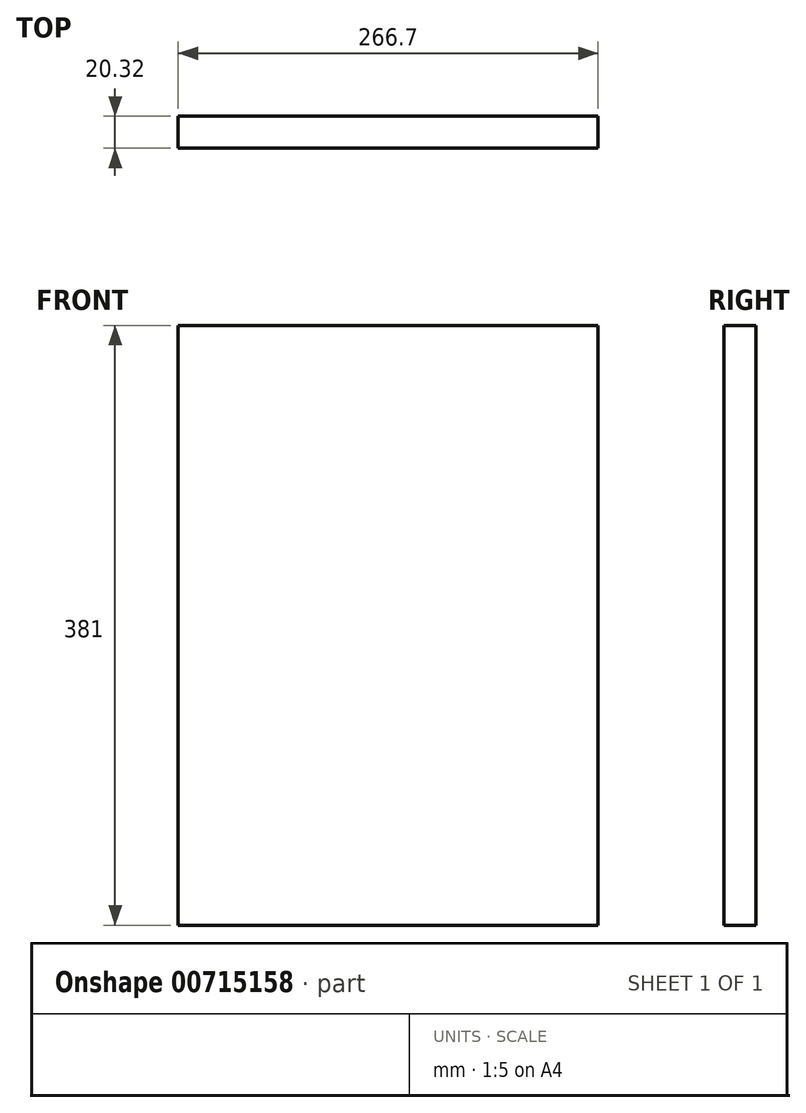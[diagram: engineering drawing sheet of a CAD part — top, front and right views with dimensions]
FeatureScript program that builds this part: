
annotation { "Feature Type Name" : "Feature", "Feature Type Description" : "" }
export const myFeature = defineFeature(function(context is Context, id is Id, definition is map)
    precondition{}
    {
        {
            var Q0;
            Q0=qCreatedBy(makeId("Front.planeOp"),FACE);
            var sketch = newSketch(context, id + "F0", { "sketchPlane" : qUnion([Q0])});
            skLineSegment(sketch, "E0.bottom", {"start": v(-142.27, 239.95) * mm, "end": v(124.43, 239.95) * mm});
            skLineSegment(sketch, "E0.top", {"start": v(-142.27, -141.05) * mm, "end": v(124.43, -141.05) * mm});
            skLineSegment(sketch, "E0.left", {"start": v(-142.27, 239.95) * mm, "end": v(-142.27, -141.05) * mm});
            skLineSegment(sketch, "E0.right", {"start": v(124.43, 239.95) * mm, "end": v(124.43, -141.05) * mm});
            skSolve(sketch);
        }
        {
            var Q0;
            Q0=makeQuery(id+"F0.imprint","IMPRINT",FACE,{"disambiguationData":[TD([[makeQuery(id+"F0.imprint","IMPRINT",EDGE,{"derivedFrom":sQuery(id+"F0.wireOp",EDGE,"E0.bottom")}),-1.0]])]});
            extrude(context, id + "F1", {"entities" : qUnion([Q0]), "depth" : 20.32 * mm, "offsetDistance" : 25.4 * mm});
        }
    });
